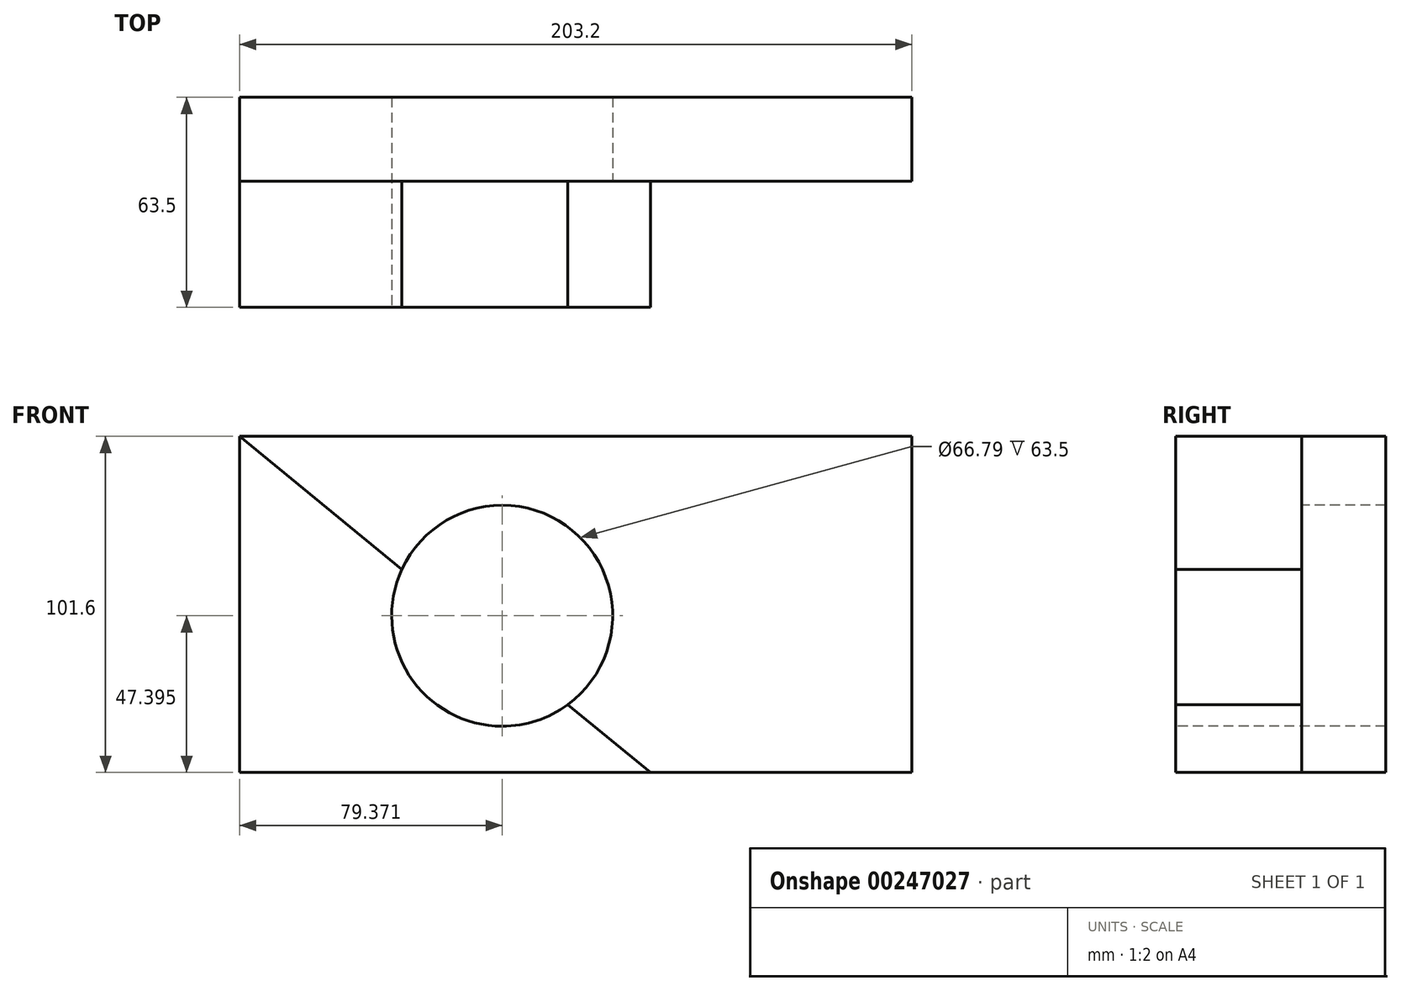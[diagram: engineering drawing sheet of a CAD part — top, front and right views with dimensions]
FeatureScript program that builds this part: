
annotation { "Feature Type Name" : "Feature", "Feature Type Description" : "" }
export const myFeature = defineFeature(function(context is Context, id is Id, definition is map)
    precondition{}
    {
        {
            var Q0;
            Q0=qCreatedBy(makeId("Front.planeOp"),FACE);
            var sketch = newSketch(context, id + "F0", { "sketchPlane" : qUnion([Q0])});
            skLineSegment(sketch, "E0.bottom", {"start": v(-124.19, -7.26) * mm, "end": v(79.01, -7.26) * mm});
            skLineSegment(sketch, "E0.top", {"start": v(-124.19, 94.34) * mm, "end": v(79.01, 94.34) * mm});
            skLineSegment(sketch, "E0.left", {"start": v(-124.19, -7.26) * mm, "end": v(-124.19, 94.34) * mm});
            skLineSegment(sketch, "E0.right", {"start": v(79.01, -7.26) * mm, "end": v(79.01, 94.34) * mm});
            skSolve(sketch);
        }
        {
            var Q0;
            Q0 = qSketchRegion(id + "F0", true);
            extrude(context, id + "F1", {"entities" : qUnion([Q0]), "depth" : 25.4 * mm});
        }
        {
            var Q0;
            Q0=makeQuery(id+"F1.opExtrude","CAP_FACE",FACE,{"disambiguationData":[OSD([sQuery(id+"F0.wireOp",EDGE,"E0.bottom"),sQuery(id+"F0.wireOp",EDGE,"E0.top"),sQuery(id+"F0.wireOp",EDGE,"E0.left"),sQuery(id+"F0.wireOp",EDGE,"E0.right")])],"isStart":false});
            var sketch = newSketch(context, id + "F2", { "sketchPlane" : qUnion([Q0])});
            skLineSegment(sketch, "E1", {"start": v(-124.19, 94.34) * mm, "end": v(-124.19, -7.26) * mm});
            skLineSegment(sketch, "E2", {"start": v(-124.19, -7.26) * mm, "end": v(0, -7.26) * mm});
            skLineSegment(sketch, "E3", {"start": v(0, -7.26) * mm, "end": v(-124.19, 94.34) * mm});
            skSolve(sketch);
        }
        {
            var Q0;
            Q0 = qSketchRegion(id + "F2", true);
            extrude(context, id + "F3", {"entities" : qUnion([Q0]), "operationType" : NewBodyOperationType.ADD, "depth" : 38.1 * mm});
        }
        {
            var Q0;
            Q0=makeQuery(id+"F3.opExtrude","CAP_FACE",FACE,{"disambiguationData":[OSD([sQuery(id+"F2.wireOp",EDGE,"E1"),sQuery(id+"F2.wireOp",EDGE,"E2"),sQuery(id+"F2.wireOp",EDGE,"E3")])],"isStart":false});
            var sketch = newSketch(context, id + "F4", { "sketchPlane" : qUnion([Q0])});
            skCircle(sketch, "E4", {"center": v(-44.82, 40.13) * mm, "radius": 33.4 * mm});
            skSolve(sketch);
        }
        {
            var Q0;
            Q0 = qSketchRegion(id + "F4", true);
            extrude(context, id + "F5", {"entities" : qUnion([Q0]), "operationType" : NewBodyOperationType.REMOVE, "oppositeDirection" : true, "depth" : 134.62 * mm});
        }
    });
